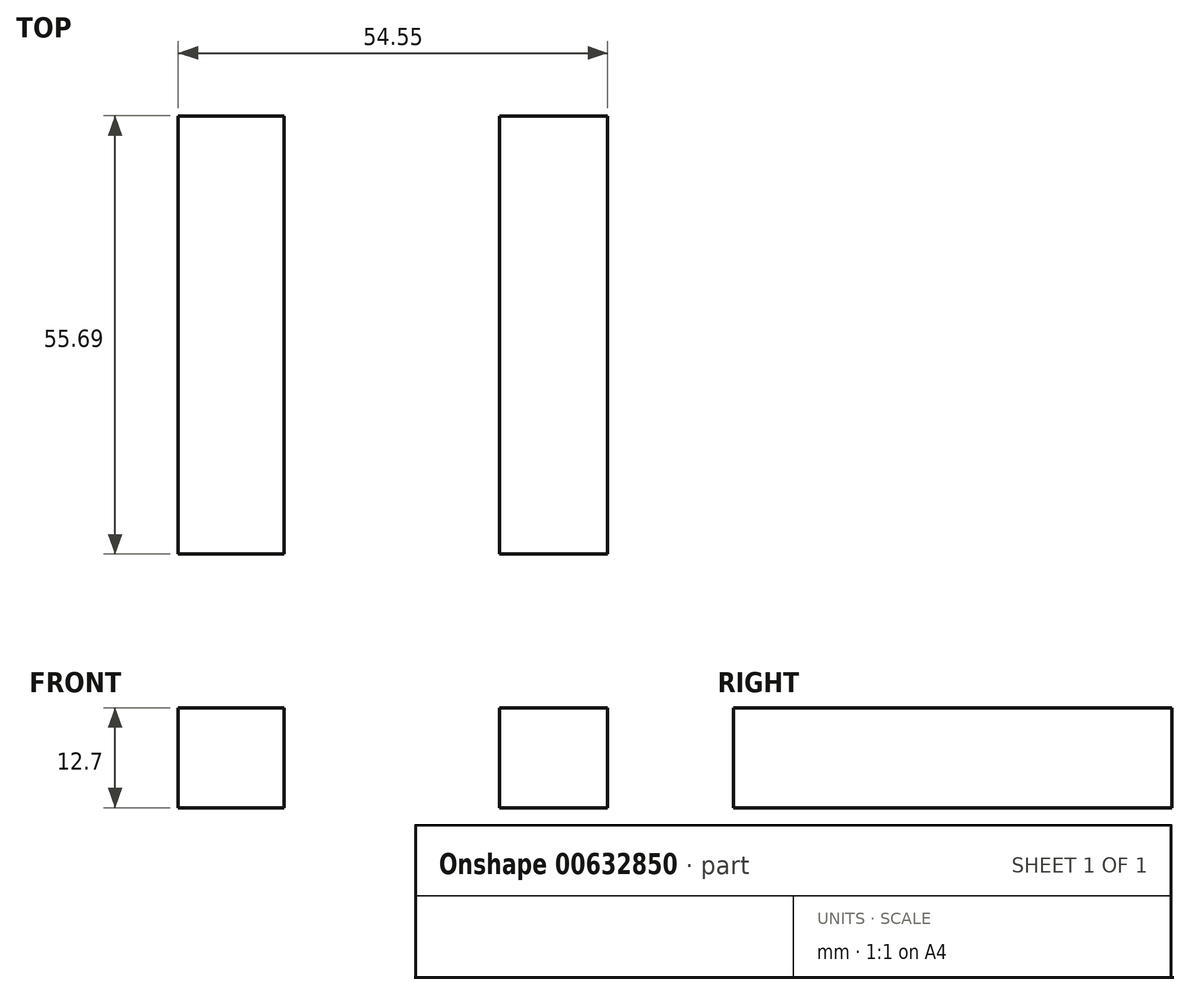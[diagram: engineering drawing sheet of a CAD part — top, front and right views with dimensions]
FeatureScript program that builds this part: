
annotation { "Feature Type Name" : "Feature", "Feature Type Description" : "" }
export const myFeature = defineFeature(function(context is Context, id is Id, definition is map)
    precondition{}
    {
        {
            var Q0;
            Q0=qCreatedBy(makeId("Top.planeOp"),FACE);
            var sketch = newSketch(context, id + "F0", { "sketchPlane" : qUnion([Q0])});
            skLineSegment(sketch, "E0.bottom", {"start": v(-22.42, 26.99) * mm, "end": v(32.13, 26.99) * mm});
            skLineSegment(sketch, "E0.top", {"start": v(-22.42, -28.7) * mm, "end": v(32.13, -28.7) * mm});
            skLineSegment(sketch, "E0.left", {"start": v(-22.42, 26.99) * mm, "end": v(-22.42, -28.7) * mm});
            skLineSegment(sketch, "E0.right", {"start": v(32.13, 26.99) * mm, "end": v(32.13, -28.7) * mm});
            skLineSegment(sketch, "E1.bottom", {"start": v(-22.42, 26.99) * mm, "end": v(-9, 26.99) * mm});
            skLineSegment(sketch, "E1.top", {"start": v(-22.42, -28.7) * mm, "end": v(-9, -28.7) * mm});
            skLineSegment(sketch, "E1.right", {"start": v(-9, 26.99) * mm, "end": v(-9, -28.7) * mm});
            skLineSegment(sketch, "E2.bottom", {"start": v(18.42, 26.99) * mm, "end": v(32.13, 26.99) * mm});
            skLineSegment(sketch, "E2.top", {"start": v(18.42, 26.99) * mm, "end": v(32.13, 26.99) * mm});
            skLineSegment(sketch, "E2.left", {"start": v(18.42, 26.99) * mm, "end": v(18.42, 26.99) * mm});
            skLineSegment(sketch, "E2.right", {"start": v(32.13, 26.99) * mm, "end": v(32.13, 26.99) * mm});
            skLineSegment(sketch, "E3.bottom", {"start": v(32.13, -28.7) * mm, "end": v(18.42, -28.7) * mm});
            skLineSegment(sketch, "E3.top", {"start": v(32.13, 26.99) * mm, "end": v(18.42, 26.99) * mm});
            skLineSegment(sketch, "E3.left", {"start": v(32.13, -28.7) * mm, "end": v(32.13, 26.99) * mm});
            skLineSegment(sketch, "E3.right", {"start": v(18.42, -28.7) * mm, "end": v(18.42, 26.99) * mm});
            skCircle(sketch, "E4", {"center": v(4.57, 19.28) * mm, "radius": 3.27 * mm});
            skCircle(sketch, "E5", {"center": v(4.21, -17.46) * mm, "radius": 2.97 * mm});
            skSolve(sketch);
        }
        {
            var Q0;
            Q0=makeQuery(id+"F0.imprint","IMPRINT",FACE,{"disambiguationData":[TD([[makeQuery(id+"F0.imprint","IMPRINT",EDGE,{"derivedFrom":sQuery(id+"F0.wireOp",EDGE,"E0.bottom")}),-1.0]])]});
            extrude(context, id + "F1", {"entities" : qUnion([Q0]), "depth" : 12.7 * mm, "offsetDistance" : 25.4 * mm});
        }
    });
